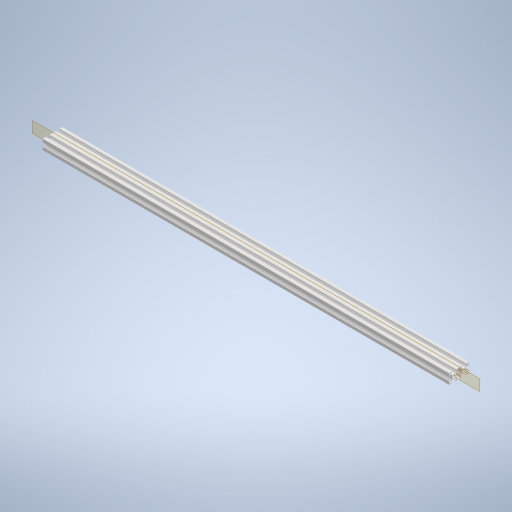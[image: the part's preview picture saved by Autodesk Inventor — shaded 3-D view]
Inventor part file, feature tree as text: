
AUTODESK INVENTOR PART (.ipt)
format: ipt  version: 2023 (Build 270158000, 158)  size: 422,912 bytes
history: native  units: mm
features: mirror x4, extrude x2, sketch x2, plane x1
ambient origin geometry x8: Origin, YZ Plane, XZ Plane, XY Plane, X Axis, Y Axis, Z Axis, Center Point
bodies: Solid1 (feature_tree)
feature tree (9):
  extrude  "Extrusion1"  Depth=10.0mm
  mirror  "Mirror1"
  mirror  "Mirror2"
  extrude  "Extrusion2"  Depth=0.5mm
  mirror  "Mirror4"
  plane  "Work Plane1"
  mirror  "Mirror5"
  sketch  "Sketch1"  dims[d1=0.5mm d2=10.0mm]
  sketch  "Sketch2"  dims[d3=5.5mm d4=3.7mm d5=2.5mm d8=10.0mm d9=1.5mm d11=6.2mm d12=135.0deg d13=1.5mm d14=800.0mm d15=0.0mm d16=135.0deg d17=90.0deg d18=0.5mm d19=0.5mm d20=1.0mm d21=1.5mm d22=10.0mm d23=11.0mm d24=7.4mm d25=6.4mm d26=10.0mm d27=800.0mm d28=0.0mm d29=0.5mm d30=0.872665mm d31=0.5mm d32=0.872665mm]
